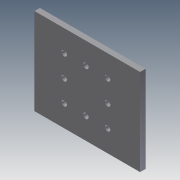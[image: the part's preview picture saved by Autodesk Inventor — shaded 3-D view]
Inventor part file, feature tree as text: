
AUTODESK INVENTOR PART (.ipt)
format: ipt  version: 2011 (Build 150239000, 239)  size: 118,272 bytes
history: native  units: in
note: dims shown in document units (in); Inventor stores cm internally (conversion verified against a paired STEP export)
features: extrude x5, sketch x5
ambient origin geometry x8: Origin, YZ Plane, XZ Plane, XY Plane, X Axis, Y Axis, Z Axis, Center Point
bodies: Solid1 (feature_tree)
feature tree (10):
  extrude  "Extrusion1"  Depth=1.1811in
  extrude  "Extrusion2"  Depth=0.315in
  extrude  "Extrusion3"  Depth=0.6299in
  extrude  "Extrusion4"  Depth=0.6299in
  extrude  "Extrusion6"  Depth=0.0787in TaperAngle=0.0deg
  sketch  "Sketch1"  dims[d0=1.5748in d1=1.1811in]
  sketch  "Sketch2"  dims[d2=0.0787in d3=0.0in d4=0.315in]
  sketch  "Sketch3"  dims[d5=0.315in d6=0.6299in]
  sketch  "Sketch4"  dims[d7=0.6299in d8=0.6299in]
  sketch  "Sketch7"  dims[d9=0.0787in d10=0.0787in d11=0.0in d12=0.0394in d13=0.0in d14=0.0394in d15=0.0in d18=0.0394in d19=2.0in d20=0.0in]
